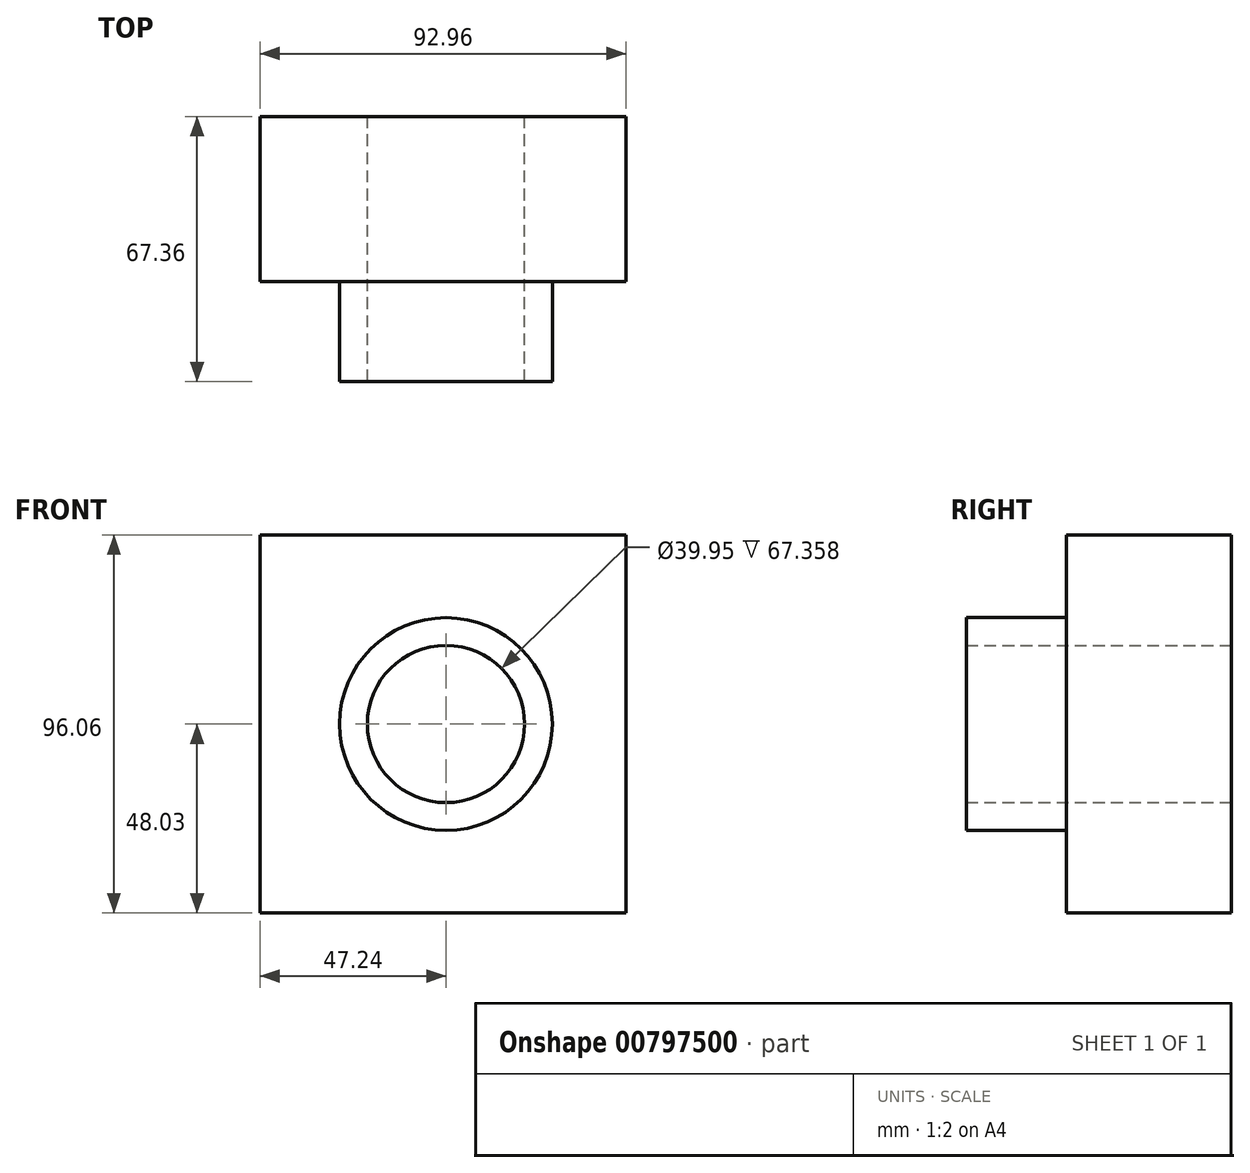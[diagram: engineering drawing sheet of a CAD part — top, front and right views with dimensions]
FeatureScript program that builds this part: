
annotation { "Feature Type Name" : "Feature", "Feature Type Description" : "" }
export const myFeature = defineFeature(function(context is Context, id is Id, definition is map)
    precondition{}
    {
        {
            var Q0;
            Q0=qCreatedBy(makeId("Right.planeOp"),FACE);
            var sketch = newSketch(context, id + "F0", { "sketchPlane" : qUnion([Q0])});
            skLineSegment(sketch, "E0.bottom", {"start": v(20.98, 48.03) * mm, "end": v(-20.98, 48.03) * mm});
            skLineSegment(sketch, "E0.top", {"start": v(20.98, -48.03) * mm, "end": v(-20.98, -48.03) * mm});
            skLineSegment(sketch, "E0.left", {"start": v(20.98, 48.03) * mm, "end": v(20.98, -48.03) * mm});
            skLineSegment(sketch, "E0.right", {"start": v(-20.98, 48.03) * mm, "end": v(-20.98, -48.03) * mm});
            skPoint(sketch, "E0.middle", {"position": v(0, 0) * mm});
            skSolve(sketch);
        }
        {
            var Q0;
            Q0 = qSketchRegion(id + "F0", true);
            extrude(context, id + "F1", {"entities" : qUnion([Q0]), "depth" : 45.72 * mm, "offsetDistance" : 25.4 * mm});
        }
        {
            var Q0;
            Q0=makeQuery(id+"F1.opExtrude","CAP_FACE",FACE,{"disambiguationData":[OSD([sQuery(id+"F0.wireOp",EDGE,"E0.bottom"),sQuery(id+"F0.wireOp",EDGE,"E0.top"),sQuery(id+"F0.wireOp",EDGE,"E0.left"),sQuery(id+"F0.wireOp",EDGE,"E0.right")])],"isStart":true});
            extrude(context, id + "F2", {"entities" : qUnion([Q0]), "operationType" : NewBodyOperationType.ADD, "depth" : 47.24 * mm, "offsetDistance" : 25.4 * mm});
        }
        {
            var Q0;
            {var subQ0=sQuery(id+"F0.wireOp",EDGE,"E0.right");Q0=makeQuery(id+"F2.boolean.opBoolean","MERGE",FACE,{"derivedFrom":[makeQuery(id+"F1.opExtrude","SWEPT_FACE",FACE,{"disambiguationData":[OSD([subQ0])]}),makeQuery(id+"F2.opExtrude","SWEPT_FACE",FACE,{"disambiguationData":[OSD([subQ0])]})]});}
            var sketch = newSketch(context, id + "F3", { "sketchPlane" : qUnion([Q0])});
            skCircle(sketch, "E1", {"center": v(0, 0) * mm, "radius": 27.01 * mm});
            skCircle(sketch, "E2", {"center": v(0, 0) * mm, "radius": 19.97 * mm});
            skSolve(sketch);
        }
        {
            var Q0;
            Q0=makeQuery(id+"F3.imprint","IMPRINT",FACE,{"disambiguationData":[TD([[makeQuery(id+"F3.imprint","IMPRINT",EDGE,{"derivedFrom":sQuery(id+"F3.wireOp",EDGE,"E1")}),1.0]])]});
            extrude(context, id + "F4", {"entities" : qUnion([Q0]), "operationType" : NewBodyOperationType.ADD, "depth" : 25.4 * mm, "offsetDistance" : 25.4 * mm});
        }
        {
            var Q0;
            {var subQ0=sQuery(id+"F0.wireOp",EDGE,"E0.right");Q0=makeQuery(id+"F4.boolean.opBoolean","SPLIT",FACE,{"disambiguationData":[TD([makeQuery(id+"F4.opExtrude","SWEPT_FACE",FACE,{"disambiguationData":[OSD([sQuery(id+"F3.wireOp",EDGE,"E2")])]})])],"derivedFrom":makeQuery(id+"F2.boolean.opBoolean","MERGE",FACE,{"derivedFrom":[makeQuery(id+"F1.opExtrude","SWEPT_FACE",FACE,{"disambiguationData":[OSD([subQ0])]}),makeQuery(id+"F2.opExtrude","SWEPT_FACE",FACE,{"disambiguationData":[OSD([subQ0])]})]})});}
            extrude(context, id + "F5", {"entities" : qUnion([Q0]), "operationType" : NewBodyOperationType.REMOVE, "oppositeDirection" : true, "depth" : 76.7 * mm, "offsetDistance" : 25.4 * mm});
        }
    });
